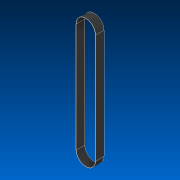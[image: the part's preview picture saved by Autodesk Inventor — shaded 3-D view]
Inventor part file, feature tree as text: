
AUTODESK INVENTOR PART (.ipt)
format: ipt  version: 2022.2 (Build 262287000, 287)  size: 92,160 bytes
history: native  units: in
note: dims shown in document units (in); Inventor stores cm internally (conversion verified against a paired STEP export)
features: extrude x1, sketch x1
ambient origin geometry x8: Origin, YZ Plane, XZ Plane, XY Plane, X Axis, Y Axis, Z Axis, Center Point
bodies: Solid1 (feature_tree)
feature tree (2):
  extrude  "Extrusion1"  Depth=0.0625in
  sketch  "Sketch1"  dims[d0=19.5in d2=0.0625in d3=1.5in d4=0.0in d5=3.5in]
